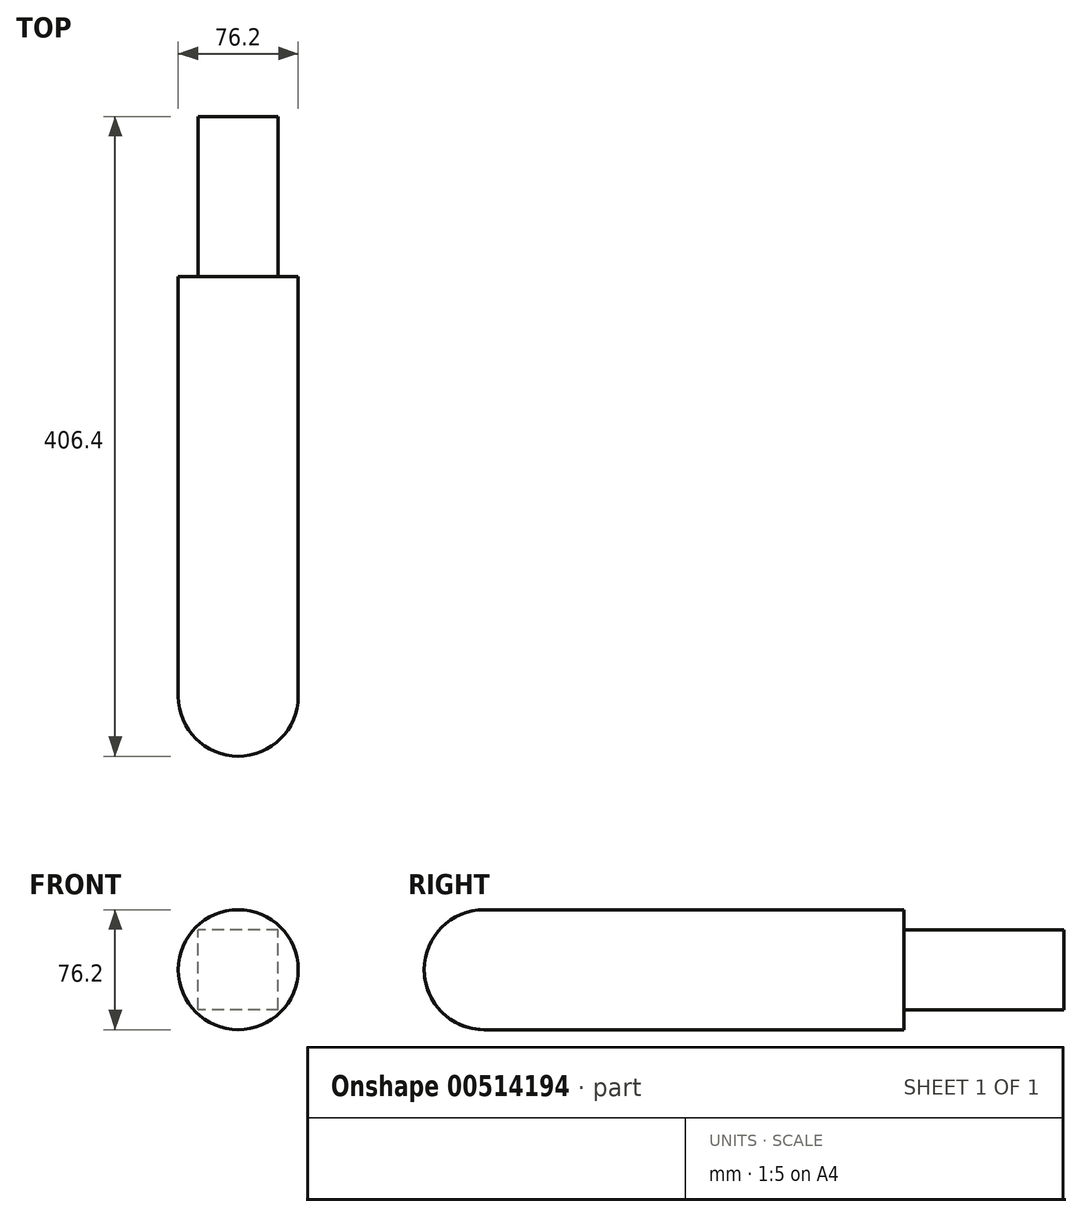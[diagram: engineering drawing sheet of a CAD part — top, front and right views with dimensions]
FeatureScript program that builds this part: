
annotation { "Feature Type Name" : "Feature", "Feature Type Description" : "" }
export const myFeature = defineFeature(function(context is Context, id is Id, definition is map)
    precondition{}
    {
        {
            var Q0;
            Q0=qCreatedBy(makeId("Front.planeOp"),FACE);
            var sketch = newSketch(context, id + "F0", { "sketchPlane" : qUnion([Q0])});
            skLineSegment(sketch, "E0.bottom", {"start": v(25.4, -25.4) * mm, "end": v(-25.4, -25.4) * mm});
            skLineSegment(sketch, "E0.top", {"start": v(25.4, 25.4) * mm, "end": v(-25.4, 25.4) * mm});
            skLineSegment(sketch, "E0.left", {"start": v(25.4, -25.4) * mm, "end": v(25.4, 25.4) * mm});
            skLineSegment(sketch, "E0.right", {"start": v(-25.4, -25.4) * mm, "end": v(-25.4, 25.4) * mm});
            skPoint(sketch, "E0.middle", {"position": v(0, 0) * mm});
            skSolve(sketch);
        }
        {
            var Q0;
            Q0=makeQuery(id+"F0.imprint","IMPRINT",FACE,{"disambiguationData":[TD([[makeQuery(id+"F0.imprint","IMPRINT",EDGE,{"derivedFrom":sQuery(id+"F0.wireOp",EDGE,"E0.bottom")}),-1.0]])]});
            extrude(context, id + "F1", {"entities" : qUnion([Q0]), "depth" : 101.6 * mm, "offsetDistance" : 25.4 * mm});
        }
        {
            var Q0;
            Q0=makeQuery(id+"F1.opExtrude","CAP_FACE",FACE,{"disambiguationData":[OSD([sQuery(id+"F0.wireOp",EDGE,"E0.bottom"),sQuery(id+"F0.wireOp",EDGE,"E0.top"),sQuery(id+"F0.wireOp",EDGE,"E0.left"),sQuery(id+"F0.wireOp",EDGE,"E0.right")])],"isStart":false});
            var sketch = newSketch(context, id + "F2", { "sketchPlane" : qUnion([Q0])});
            skCircle(sketch, "E1", {"center": v(0, 0) * mm, "radius": 38.1 * mm});
            skSolve(sketch);
        }
        {
            var Q0;
            Q0=makeQuery(id+"F2.imprint","IMPRINT",FACE,{"disambiguationData":[TD([[makeQuery(id+"F2.imprint","IMPRINT",EDGE,{"derivedFrom":sQuery(id+"F2.wireOp",EDGE,"E1")}),1.0]])]});
            var Q1;
            Q1=makeQuery(id+"F2.imprint","IMPRINT",FACE,{"disambiguationData":[TD([[makeQuery(id+"F2.imprint","IMPRINT",EDGE,{"derivedFrom":makeQuery(id+"F1.opExtrude","CAP_EDGE",EDGE,{"disambiguationData":[OSD([sQuery(id+"F0.wireOp",EDGE,"E0.bottom")])],"isStart":false})}),-1.0]])]});
            var Q2;
            Q2=sQuery(id+"F2.wireOp",EDGE,"E1");
            extrude(context, id + "F3", {"entities" : qUnion([Q0, Q1]), "operationType" : NewBodyOperationType.ADD, "surfaceEntities" : qUnion([Q2]), "depth" : 304.8 * mm, "offsetDistance" : 25.4 * mm});
        }
        {
            var Q0;
            Q0=makeQuery(id+"F3.opExtrude","CAP_EDGE",EDGE,{"disambiguationData":[OSD([sQuery(id+"F2.wireOp",EDGE,"E1")])],"isStart":false});
            fillet(context, id + "F4", {"entities" : qUnion([Q0]), "radius" : 38.1 * mm, "tangentPropagation" : true, "allowEdgeOverflow" : false});
        }
    });
